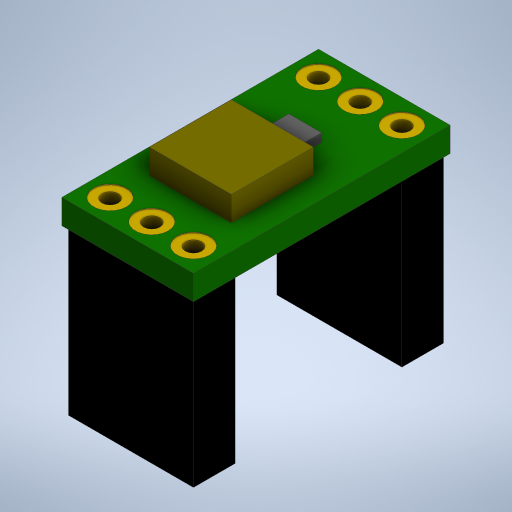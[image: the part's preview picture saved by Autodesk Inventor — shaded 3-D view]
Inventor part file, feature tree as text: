
AUTODESK INVENTOR PART (.ipt)
format: ipt  version: 2024.1 (Build 281209000, 209)  size: 308,736 bytes
history: native  units: mm
features: extrude x6, sketch x3, projected_geometry x2, other x1
ambient origin geometry x8: Origin, YZ Plane, XZ Plane, XY Plane, X Axis, Y Axis, Z Axis, Center Point
bodies: Body1 (feature_tree)
feature tree (12):
  other  "ソリッド1"
  extrude  "押し出し1"  Depth=7.62mm
  extrude  "押し出し2"  Depth=2.54mm
  sketch  "スケッチ3"
  extrude  "押し出し3"  Depth=12.7mm
  extrude  "押し出し4"  Depth=10.0mm TaperAngle=0.0deg
  extrude  "押し出し5"  Depth=1.5mm TaperAngle=0.0deg
  extrude  "押し出し6"  Depth=0.2mm
  sketch  "スケッチ1"
  sketch  "スケッチ2"
  projected_geometry  "投影ループ1"
  projected_geometry  "投影ループ2"
